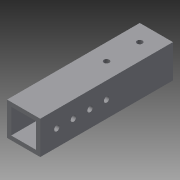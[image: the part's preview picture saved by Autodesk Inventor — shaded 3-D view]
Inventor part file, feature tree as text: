
AUTODESK INVENTOR PART (.ipt)
format: ipt  version: 2014 (Build 180170000, 170)  size: 106,496 bytes
history: native  units: in
note: dims shown in document units (in); Inventor stores cm internally (conversion verified against a paired STEP export)
features: extrude x3, sketch x3
ambient origin geometry x8: Origin, YZ Plane, XZ Plane, XY Plane, X Axis, Y Axis, Z Axis, Center Point
bodies: Solid1 (feature_tree)
feature tree (6):
  extrude  "Extrusion1"  Depth=1.0in
  extrude  "Extrusion2"  Depth=4.0in TaperAngle=0.0deg
  extrude  "Extrusion3"  Depth=4.0in
  sketch  "Sketch1"  dims[d0=1.0in d1=1.0in]
  sketch  "Sketch2"  dims[d2=0.125in d3=4.0in d4=0.0in]
  sketch  "Sketch3"  dims[d5=0.163in d6=0.5in d7=0.5in d8=1.5748in d10=0.5in d11=0.3937in d13=1.0in d15=4.0in d16=0.0in d17=0.163in d18=0.5in d19=0.5in d20=0.7874in d22=1.0in d23=0.3937in d25=1.0in d27=4.0in d28=0.0in]
